# Revit family: Cleanout_Floor_Heavy-duty _Non-Adjustable_Zurn-Z1402
name_source: partatom
category: Plumbing Fixtures
units: mm (PartAtom-declared; Revit-internal decimal feet)

## family parameters
Always vertical = Yes
Cut with Voids When Loaded = No
Maintain Annotation Orientation = No
OmniClass Number = 23.45.55.21
OmniClass Title = Drains (Wastes)
Part Type = Normal
Room Calculation Point = No
Round Connector Dimension = Use Radius
Shared = No
Work Plane-Based = No

## types (40) — shared parameters
Assembly Code = D2030100
CW Connection = No
Default Elevation = 20 "
Description = HEAVY-DUTY NON-ADJUSTABLE FLOOR CLEANOUT
HW Connection = No
Main Material = Iron - Zurn -Cast - Painted - Blue
Manufacturer = Zurn Water, LLC
Manufacurer Brand = Zurn
Modified Date = 09/19/2025
Product Documentation Link = https://files.zurn.com
Product Installation Sheet = https://files.zurn.com
Product Page URL = https://www.zurn.com
Product data url = https://www.bimobject.com
URL = www.zurn.com
Vent Connection = No
WFU = 1
Waste Connection = Yes
zero-valued in all types: CWFU, HWFU

## per-type parameters (varying)
| type | Approx. Weight (Lbs) | Body Height (E) | Frame Height | Frame and Grate | Grate Radius | Inside Radius | Inside Revolve | Model | NH | Outlet Connector Radius | Pipe Size A (Actual) | Pipe Size A (Nominal) | Type Comments | Width C |
| Z1402-2NL Outlet | 5 " | 3.5 " | 0.875 " | Iron - Zurn -Cast - Painted - Blue | 1.75 " | 1.82 " | 0.25 " | Z1402 | No | 1 " | 1.188 " | 1 " | Z1402-2 Inch -Neo Loc Outlet | 2.063 " |
| Z1402-3NH Outlet | 5 " | 3.5 " | 0.875 " | Iron - Zurn -Cast - Painted - Blue | 1.75 " | 1.82 " | 0.25 " | Z1402 | Yes | 1.5 " | 1.75 " | 1.5 " | Z1402-3 Inch -No Hub Outlet | 2.063 " |
| Z1402-3NL Outlet | 8 " | 3.625 " | 0.875 " | Iron - Zurn -Cast - Painted - Blue | 2.25 " | 2.32 " | 0.25 " | Z1402 | No | 1.5 " | 1.75 " | 1.5 " | Z1402-3 Inch -Neo Loc Outlet | 2.563 " |
| Z1402-4NL Outlet | 8 " | 3.625 " | 0.875 " | Iron - Zurn -Cast - Painted - Blue | 2.75 " | 2.82 " | 0.25 " | Z1402 | No | 2 " | 2.25 " | 2 " | Z1402-4 Inch -Neo Loc Outlet | 3.063 " |
| Z1402-4NH Outlet | 10 " | 3.625 " | 0.875 " | Iron - Zurn -Cast - Painted - Blue | 2.25 " | 2.32 " | 0.25 " | Z1402 | Yes | 1.5 " | 2.25 " | 2 " | Z1402-4 Inch -No Hub Outlet | 2.563 " |
| Z1402-5NL Outlet | 15 " | 3.75 " | 0.875 " | Iron - Zurn -Cast - Painted - Blue | 3.312 " | 3.382 " | 0.25 " | Z1402 | No | 2.5 " | 2.782 " | 2.5 " | Z1402-5 Inch -Neo Loc Outlet | 3.625 " |
| Z1402-6NL Outlet | 17 " | 3.75 " | 0.875 " | Iron - Zurn -Cast - Painted - Blue | 3.812 " | 3.882 " | 0.25 " | Z1402 | No | 3 " | 3.313 " | 3 " | Z1402-6 Inch -Neo Loc Outlet | 4.125 " |
| Z1402-6NH Outlet | 15 " | 3.75 " | 0.875 " | Iron - Zurn -Cast - Painted - Blue | 3.312 " | 3.382 " | 0.25 " | Z1402 | Yes | 3 " | 3.313 " | 3 " | Z1402-6 Inch -No Hub Outlet | 3.625 " |
| Z1402-8NH Outlet | 22 " | 3.75 " | 0.875 " | Iron - Zurn -Cast - Painted - Blue | 4.312 " | 4.382 " | 0.25 " | Z1402 | Yes | 4 " | 4.313 " | 4 " | Z1402-8 Inch -No Hub Outlet | 4.625 " |
| Z1402-8NL Outlet | 22 " | 3.75 " | 0.875 " | Iron - Zurn -Cast - Painted - Blue | 4.312 " | 4.382 " | 0.25 " | Z1402 | No | 4 " | 4.313 " | 4 " | Z1402-8 Inch -Neo Loc Outlet | 4.625 " |
| ZS1402-2NL Outlet | 5 " | 3.5 " | 1.063 " | Steel - Zurn - Stainless-Polished | 1.75 " | 1.82 " | 0.25 " | ZS1402 | No | 1 " | 1.188 " | 1 " | ZS1402-2 Inch -Neo Loc Outlet | 2.063 " |
| ZS1402-3NH Outlet | 5 " | 3.5 " | 1.063 " | Steel - Zurn - Stainless-Polished | 1.75 " | 1.82 " | 0.25 " | ZS1402 | Yes | 1.5 " | 1.75 " | 1.5 " | ZS1402-3 Inch -No Hub Outlet | 2.063 " |
| ZS1402-3NL Outlet | 8 " | 3.625 " | 1.063 " | Steel - Zurn - Stainless-Polished | 2.25 " | 2.32 " | 0.25 " | ZS1402 | No | 1.5 " | 1.75 " | 1.5 " | ZS1402-3 Inch -Neo Loc Outlet | 2.563 " |
| ZS1402-4NL Outlet | 8 " | 3.625 " | 1.063 " | Steel - Zurn - Stainless-Polished | 2.75 " | 2.82 " | 0.25 " | ZS1402 | No | 2 " | 2.25 " | 2 " | ZS1402-4 Inch -Neo Loc Outlet | 3.063 " |
| ZS1402-4NH Outlet | 10 " | 3.625 " | 1.063 " | Steel - Zurn - Stainless-Polished | 2.25 " | 2.32 " | 0.25 " | ZS1402 | Yes | 1.5 " | 2.25 " | 2 " | ZS1402-4 Inch -No Hub Outlet | 2.563 " |
| ZS1402-5NL Outlet | 15 " | 3.75 " | 1.063 " | Steel - Zurn - Stainless-Polished | 3.312 " | 3.382 " | 0.25 " | ZS1402 | No | 2.5 " | 2.782 " | 2.5 " | ZS1402-5 Inch -Neo Loc Outlet | 3.625 " |
| ZS1402-6NL Outlet | 17 " | 3.75 " | 1.063 " | Steel - Zurn - Stainless-Polished | 3.812 " | 3.882 " | 0.25 " | ZS1402 | No | 3 " | 3.313 " | 3 " | ZS1402-6 Inch -Neo Loc Outlet | 4.125 " |
| ZS1402-6NH Outlet | 15 " | 3.75 " | 1.063 " | Steel - Zurn - Stainless-Polished | 3.312 " | 3.382 " | 0.25 " | ZS1402 | Yes | 3 " | 3.313 " | 3 " | ZS1402-6 Inch -No Hub Outlet | 3.625 " |
| ZS1402-8NH Outlet | 22 " | 3.75 " | 1.063 " | Steel - Zurn - Stainless-Polished | 4.312 " | 4.382 " | 0.25 " | ZS1402 | Yes | 4 " | 4.313 " | 4 " | ZS1402-8 Inch -No Hub Outlet | 4.625 " |
| ZS1402-8NL Outlet | 22 " | 3.75 " | 1.063 " | Steel - Zurn - Stainless-Polished | 4.312 " | 4.382 " | 0.25 " | ZS1402 | No | 4 " | 4.313 " | 4 " | ZS1402-8 Inch -Neo Loc Outlet | 4.625 " |
| ZN1402-2NL Outlet | 5 " | 3.5 " | 0.375 " | Bronze - Zurn - Polished Nickel | 1.75 " | 1.82 " | 0.125 " | ZN1402 | No | 1 " | 1.188 " | 1 " | ZN1402-2 Inch -Neo Loc Outlet | 2.063 " |
| ZN1402-3NH Outlet | 5 " | 3.5 " | 0.375 " | Bronze - Zurn - Polished Nickel | 1.75 " | 1.82 " | 0.125 " | ZN1402 | Yes | 1.5 " | 1.75 " | 1.5 " | ZN1402-3 Inch -No Hub Outlet | 2.063 " |
| ZN1402-3NL Outlet | 8 " | 3.625 " | 0.375 " | Bronze - Zurn - Polished Nickel | 2.25 " | 2.32 " | 0.125 " | ZN1402 | No | 1.5 " | 1.75 " | 1.5 " | ZN1402-3 Inch -Neo Loc Outlet | 2.563 " |
| ZN1402-4NL Outlet | 8 " | 3.625 " | 0.375 " | Bronze - Zurn - Polished Nickel | 2.75 " | 2.82 " | 0.125 " | ZN1402 | No | 2 " | 2.25 " | 2 " | ZN1402-4 Inch -Neo Loc Outlet | 3.063 " |
| ZN1402-4NH Outlet | 10 " | 3.625 " | 0.375 " | Bronze - Zurn - Polished Nickel | 2.25 " | 2.32 " | 0.125 " | ZN1402 | Yes | 1.5 " | 2.25 " | 2 " | ZN1402-4 Inch -No Hub Outlet | 2.563 " |
| ZN1402-5NL Outlet | 15 " | 3.75 " | 0.375 " | Bronze - Zurn - Polished Nickel | 3.312 " | 3.382 " | 0.125 " | ZN1402 | No | 2.5 " | 2.782 " | 2.5 " | ZN1402-5 Inch -Neo Loc Outlet | 3.625 " |
| ZN1402-6NL Outlet | 17 " | 3.75 " | 0.375 " | Bronze - Zurn - Polished Nickel | 3.812 " | 3.882 " | 0.125 " | ZN1402 | No | 3 " | 3.313 " | 3 " | ZN1402-6 Inch -Neo Loc Outlet | 4.125 " |
| ZN1402-6NH Outlet | 15 " | 3.75 " | 0.375 " | Bronze - Zurn - Polished Nickel | 3.312 " | 3.382 " | 0.125 " | ZN1402 | Yes | 3 " | 3.313 " | 3 " | ZN1402-6 Inch -No Hub Outlet | 3.625 " |
| ZN1402-8NH Outlet | 22 " | 3.75 " | 0.375 " | Bronze - Zurn - Polished Nickel | 4.312 " | 4.382 " | 0.125 " | ZN1402 | Yes | 4 " | 4.313 " | 4 " | ZN1402-8 Inch -No Hub Outlet | 4.625 " |
| ZN1402-8NL Outlet | 22 " | 3.75 " | 0.375 " | Bronze - Zurn - Polished Nickel | 4.312 " | 4.382 " | 0.125 " | ZN1402 | No | 4 " | 4.313 " | 4 " | ZN1402-8 Inch -Neo Loc Outlet | 4.625 " |
| ZB1402-2NL Outlet | 5 " | 3.5 " | 0.375 " | Bronze - Zurn - Polished | 1.75 " | 1.82 " | 0.125 " | ZB1402 | No | 1 " | 1.188 " | 1 " | ZB1402-2 Inch -Neo Loc Outlet | 2.063 " |
| ZB1402-3NH Outlet | 5 " | 3.5 " | 0.375 " | Bronze - Zurn - Polished | 1.75 " | 1.82 " | 0.125 " | ZB1402 | Yes | 1.5 " | 1.75 " | 1.5 " | ZB1402-3 Inch -No Hub Outlet | 2.063 " |
| ZB1402-3NL Outlet | 8 " | 3.625 " | 0.375 " | Bronze - Zurn - Polished | 2.25 " | 2.32 " | 0.125 " | ZB1402 | No | 1.5 " | 1.75 " | 1.5 " | ZB1402-3 Inch -Neo Loc Outlet | 2.563 " |
| ZB1402-4NL Outlet | 8 " | 3.625 " | 0.375 " | Bronze - Zurn - Polished | 2.75 " | 2.82 " | 0.125 " | ZB1402 | No | 2 " | 2.25 " | 2 " | ZB1402-4 Inch -Neo Loc Outlet | 3.063 " |
| ZB1402-4NH Outlet | 10 " | 3.625 " | 0.375 " | Bronze - Zurn - Polished | 2.25 " | 2.32 " | 0.125 " | ZB1402 | Yes | 1.5 " | 2.25 " | 2 " | ZB1402-4 Inch -No Hub Outlet | 2.563 " |
| ZB1402-5NL Outlet | 15 " | 3.75 " | 0.375 " | Bronze - Zurn - Polished | 3.312 " | 3.382 " | 0.125 " | ZB1402 | No | 2.5 " | 2.782 " | 2.5 " | ZB1402-5 Inch -Neo Loc Outlet | 3.625 " |
| ZB1402-6NL Outlet | 17 " | 3.75 " | 0.375 " | Bronze - Zurn - Polished | 3.812 " | 3.882 " | 0.125 " | ZB1402 | No | 3 " | 3.313 " | 3 " | ZB1402-6 Inch -Neo Loc Outlet | 4.125 " |
| ZB1402-6NH Outlet | 15 " | 3.75 " | 0.375 " | Bronze - Zurn - Polished | 3.312 " | 3.382 " | 0.125 " | ZB1402 | Yes | 3 " | 3.313 " | 3 " | ZB1402-6 Inch -No Hub Outlet | 3.625 " |
| ZB1402-8NH Outlet | 22 " | 3.75 " | 0.375 " | Bronze - Zurn - Polished | 4.312 " | 4.382 " | 0.125 " | ZB1402 | Yes | 4 " | 4.313 " | 4 " | ZB1402-8 Inch -No Hub Outlet | 4.625 " |
| ZB1402-8NL Outlet | 22 " | 3.75 " | 0.375 " | Bronze - Zurn - Polished | 4.312 " | 4.382 " | 0.125 " | ZB1402 | No | 4 " | 4.313 " | 4 " | ZB1402-8 Inch -Neo Loc Outlet | 4.625 " |

## geometry (parser evidence)
native form markers: Revolve x1, Sweep x6
no freeform markers — native parametric forms only
